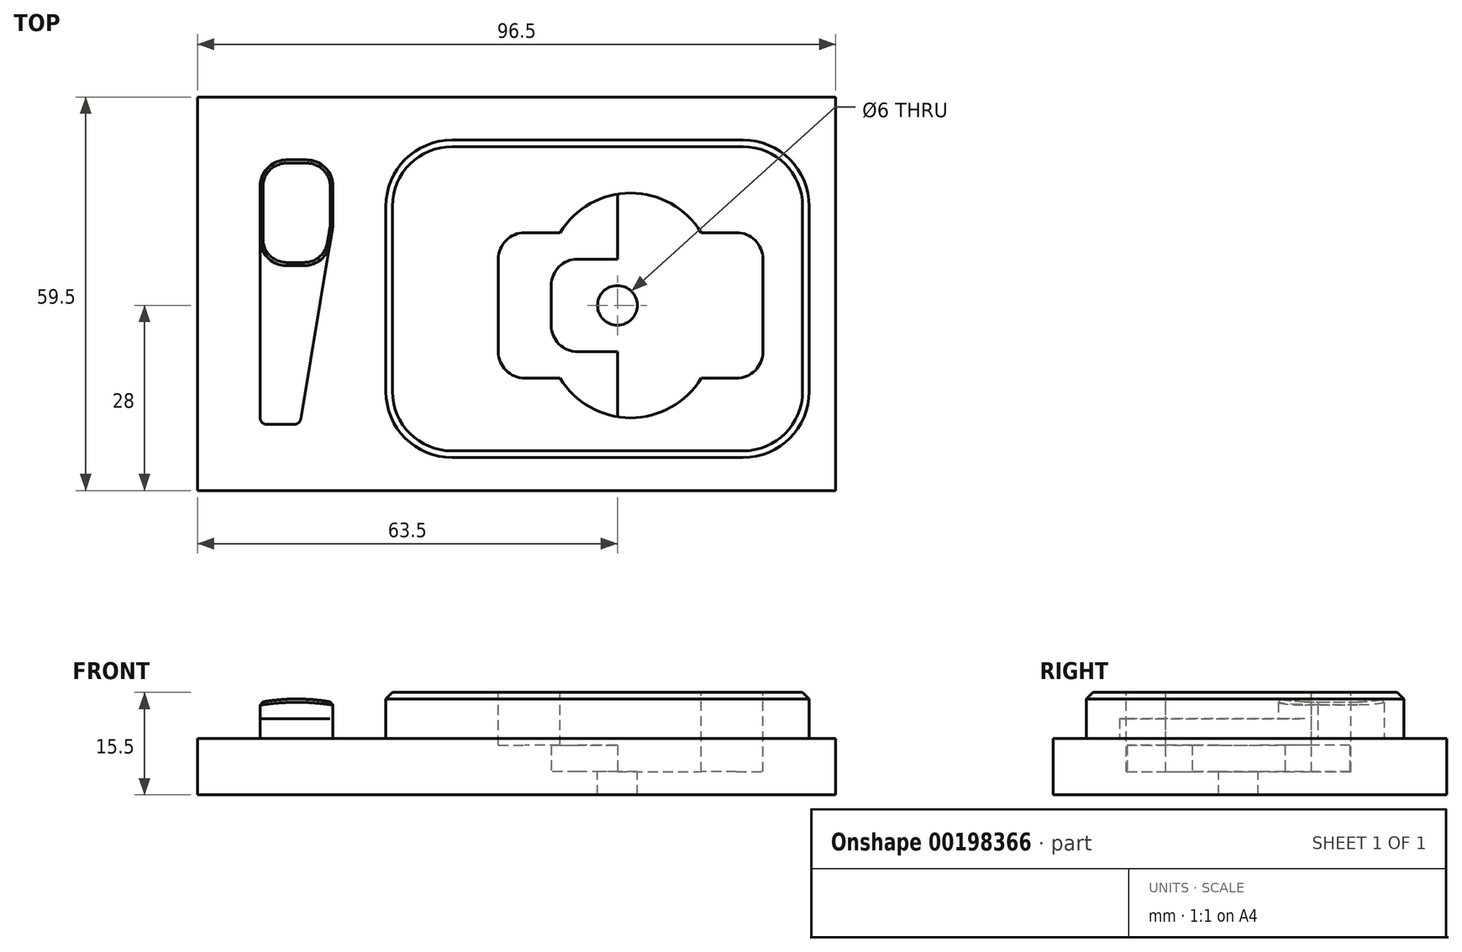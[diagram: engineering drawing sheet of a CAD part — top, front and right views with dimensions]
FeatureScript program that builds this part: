
annotation { "Feature Type Name" : "Feature", "Feature Type Description" : "" }
export const myFeature = defineFeature(function(context is Context, id is Id, definition is map)
    precondition{}
    {
        {
            var Q0;
            Q0=qCreatedBy(makeId("Top.planeOp"),FACE);
            var sketch = newSketch(context, id + "F0", { "sketchPlane" : qUnion([Q0])});
            skLineSegment(sketch, "E0.bottom", {"start": v(0, 0) * mm, "end": v(-96.5, 0) * mm});
            skLineSegment(sketch, "E0.top", {"start": v(0, 59.5) * mm, "end": v(-96.5, 59.5) * mm});
            skLineSegment(sketch, "E0.left", {"start": v(0, 0) * mm, "end": v(0, 59.5) * mm});
            skLineSegment(sketch, "E0.right", {"start": v(-96.5, 0) * mm, "end": v(-96.5, 59.5) * mm});
            skSolve(sketch);
        }
        {
            var Q0;
            Q0 = qSketchRegion(id + "F0", true);
            extrude(context, id + "F1", {"entities" : qUnion([Q0]), "oppositeDirection" : true, "depth" : 15.5 * mm, "offsetDistance" : 25 * mm});
        }
        {
            var Q0;
            Q0=makeQuery(id+"F1.opExtrude","CAP_FACE",FACE,{"disambiguationData":[OSD([sQuery(id+"F0.wireOp",EDGE,"E0.bottom"),sQuery(id+"F0.wireOp",EDGE,"E0.top"),sQuery(id+"F0.wireOp",EDGE,"E0.left"),sQuery(id+"F0.wireOp",EDGE,"E0.right")])],"isStart":true});
            var sketch = newSketch(context, id + "F2", { "sketchPlane" : qUnion([Q0])});
            skLineSegment(sketch, "E1.bottom", {"start": v(-4, 5) * mm, "end": v(-68, 5) * mm});
            skLineSegment(sketch, "E1.top", {"start": v(-4, 53) * mm, "end": v(-68, 53) * mm});
            skLineSegment(sketch, "E1.left", {"start": v(-4, 5) * mm, "end": v(-4, 53) * mm});
            skLineSegment(sketch, "E1.right", {"start": v(-68, 5) * mm, "end": v(-68, 53) * mm});
            skLineSegment(sketch, "E2.bottom", {"start": v(-11, 17) * mm, "end": v(-20.32, 17) * mm});
            skLineSegment(sketch, "E2.top", {"start": v(-11, 39) * mm, "end": v(-20.32, 39) * mm});
            skLineSegment(sketch, "E2.left", {"start": v(-11, 17) * mm, "end": v(-11, 39) * mm});
            skLineSegment(sketch, "E2.right", {"start": v(-51, 17) * mm, "end": v(-51, 39) * mm});
            skLineSegment(sketch, "E3", {"start": v(-51, 28) * mm, "end": v(-11, 28) * mm, "construction": true});
            skLineSegment(sketch, "E4", {"start": v(-31, 39) * mm, "end": v(-31, 17) * mm, "construction": true});
            skArc(sketch, "E5", {"start": v(-20.32, 17) * mm, "mid": v(-31, 11) * mm, "end": v(-41.68, 17) * mm});
            skArc(sketch, "E6.MirrorCS", {"start": v(-20.32, 39) * mm, "mid": v(-31, 45) * mm, "end": v(-41.68, 39) * mm});
            skLineSegment(sketch, "E7.trimOffspring", {"start": v(-41.68, 39) * mm, "end": v(-51, 39) * mm});
            skLineSegment(sketch, "E8.trimOffspring", {"start": v(-41.68, 17) * mm, "end": v(-51, 17) * mm});
            skSolve(sketch);
        }
        {
            var Q0;
            Q0=makeQuery(id+"F2.imprint","IMPRINT",FACE,{"disambiguationData":[TD([[makeQuery(id+"F2.imprint","IMPRINT",EDGE,{"derivedFrom":sQuery(id+"F2.wireOp",EDGE,"E1.bottom")}),1.0]])]});
            extrude(context, id + "F3", {"entities" : qUnion([Q0]), "operationType" : NewBodyOperationType.REMOVE, "oppositeDirection" : true, "depth" : (15.5 - 8.5) * mm, "offsetDistance" : 25 * mm});
        }
        {
            var Q0;
            Q0=makeQuery(id+"F2.imprint","IMPRINT",FACE,{"disambiguationData":[TD([[makeQuery(id+"F2.imprint","IMPRINT",EDGE,{"derivedFrom":sQuery(id+"F2.wireOp",EDGE,"E2.bottom")}),-1.0]])]});
            extrude(context, id + "F4", {"entities" : qUnion([Q0]), "operationType" : NewBodyOperationType.REMOVE, "oppositeDirection" : true, "depth" : 12 * mm, "offsetDistance" : 25 * mm});
        }
        {
            var Q0;
            Q0=makeQuery(id+"F4.boolean.opBoolean","COPY",FACE,{"derivedFrom":makeQuery(id+"F4.opExtrude","CAP_FACE",FACE,{"disambiguationData":[OSD([sQuery(id+"F2.wireOp",EDGE,"E2.bottom"),sQuery(id+"F2.wireOp",EDGE,"E2.top"),sQuery(id+"F2.wireOp",EDGE,"E2.left"),sQuery(id+"F2.wireOp",EDGE,"E2.right"),sQuery(id+"F2.wireOp",EDGE,"E5"),sQuery(id+"F2.wireOp",EDGE,"E6.MirrorCS"),sQuery(id+"F2.wireOp",EDGE,"E7.trimOffspring"),sQuery(id+"F2.wireOp",EDGE,"E8.trimOffspring")])],"isStart":false})});
            var sketch = newSketch(context, id + "F5", { "sketchPlane" : qUnion([Q0])});
            skLineSegment(sketch, "E9", {"start": v(-51, 28) * mm, "end": v(-11, 28) * mm, "construction": true});
            skLineSegment(sketch, "E10", {"start": v(-33, 44.84) * mm, "end": v(-33, 35) * mm});
            skLineSegment(sketch, "E11", {"start": v(-33, 35) * mm, "end": v(-43, 35) * mm});
            skLineSegment(sketch, "E12", {"start": v(-43, 35) * mm, "end": v(-43, 28) * mm});
            skLineSegment(sketch, "E13.MirrorCS", {"start": v(-43, 21) * mm, "end": v(-43, 28) * mm});
            skLineSegment(sketch, "E14.MirrorCS", {"start": v(-33, 21) * mm, "end": v(-43, 21) * mm});
            skLineSegment(sketch, "E15.MirrorCS", {"start": v(-33, 11.16) * mm, "end": v(-33, 21) * mm});
            skPoint(sketch, "E16", {"position": v(-33, 28) * mm});
            skSolve(sketch);
        }
        {
            var Q0;
            {var subQ3=sQuery(id+"F5.wireOp",EDGE,"E10");Q0=makeQuery(id+"F5.imprint","IMPRINT",FACE,{"disambiguationData":[TD([[makeQuery(id+"F5.imprint","IMPRINT",EDGE,{"derivedFrom":subQ3}),-1.0]])]});}
            extrude(context, id + "F6", {"entities" : qUnion([Q0]), "operationType" : NewBodyOperationType.ADD, "depth" : (12 - 8) * mm, "offsetDistance" : 25 * mm});
        }
        {
            var Q0;
            Q0=sQuery(id+"F5.wireOp",VERTEX,"E16");
            var Q1;
            Q1=makeQuery(id+"F1.opExtrude","SWEPT_BODY",BODY,{"disambiguationData":[OSD([sQuery(id+"F0.wireOp",EDGE,"E0.bottom"),sQuery(id+"F0.wireOp",EDGE,"E0.top"),sQuery(id+"F0.wireOp",EDGE,"E0.left"),sQuery(id+"F0.wireOp",EDGE,"E0.right")])]});
            hole(context, id + "F7", {"style" : HoleStyle.SIMPLE, "endStyle" : HoleEndStyle.THROUGH, "holeDiameter" : 6 * mm, "majorDiameter" : 5 * mm, "tappedDepth" : 12 * mm, "tapClearance" : 3, "startFromSketch" : true, "locations" : qUnion([Q0]), "scope" : qUnion([Q1])});
        }
        {
            var Q0;
            Q0=makeQuery(id+"F3.boolean.opBoolean","COPY",EDGE,{"derivedFrom":makeQuery(id+"F3.opExtrude","SWEPT_EDGE",EDGE,{"disambiguationData":[OSD([sQuery(id+"F2.wireOp",EDGE,"E1.bottom"),sQuery(id+"F2.wireOp",EDGE,"E1.right")])]})});
            var Q1;
            Q1=makeQuery(id+"F3.boolean.opBoolean","COPY",EDGE,{"derivedFrom":makeQuery(id+"F3.opExtrude","SWEPT_EDGE",EDGE,{"disambiguationData":[OSD([sQuery(id+"F2.wireOp",EDGE,"E1.bottom"),sQuery(id+"F2.wireOp",EDGE,"E1.left")])]})});
            var Q2;
            Q2=makeQuery(id+"F3.boolean.opBoolean","COPY",EDGE,{"derivedFrom":makeQuery(id+"F3.opExtrude","SWEPT_EDGE",EDGE,{"disambiguationData":[OSD([sQuery(id+"F2.wireOp",EDGE,"E1.top"),sQuery(id+"F2.wireOp",EDGE,"E1.left")])]})});
            var Q3;
            Q3=makeQuery(id+"F3.boolean.opBoolean","COPY",EDGE,{"derivedFrom":makeQuery(id+"F3.opExtrude","SWEPT_EDGE",EDGE,{"disambiguationData":[OSD([sQuery(id+"F2.wireOp",EDGE,"E1.top"),sQuery(id+"F2.wireOp",EDGE,"E1.right")])]})});
            fillet(context, id + "F8", {"entities" : qUnion([Q0, Q1, Q2, Q3]), "tangentPropagation" : true, "radius" : 10 * mm, "defaultsChanged" : false, "vertexSettings" : [], "allowEdgeOverflow" : false});
        }
        {
            var Q0;
            Q0=makeQuery(id+"F4.boolean.opBoolean","COPY",EDGE,{"derivedFrom":makeQuery(id+"F4.opExtrude","SWEPT_EDGE",EDGE,{"disambiguationData":[OSD([sQuery(id+"F2.wireOp",EDGE,"E2.right"),sQuery(id+"F2.wireOp",EDGE,"E7.trimOffspring")])]})});
            var Q1;
            Q1=makeQuery(id+"F4.boolean.opBoolean","COPY",EDGE,{"derivedFrom":makeQuery(id+"F4.opExtrude","SWEPT_EDGE",EDGE,{"disambiguationData":[OSD([sQuery(id+"F2.wireOp",EDGE,"E2.top"),sQuery(id+"F2.wireOp",EDGE,"E2.left")])]})});
            var Q2;
            Q2=makeQuery(id+"F4.boolean.opBoolean","COPY",EDGE,{"derivedFrom":makeQuery(id+"F4.opExtrude","SWEPT_EDGE",EDGE,{"disambiguationData":[OSD([sQuery(id+"F2.wireOp",EDGE,"E2.bottom"),sQuery(id+"F2.wireOp",EDGE,"E2.left")])]})});
            var Q3;
            Q3=makeQuery(id+"F4.boolean.opBoolean","COPY",EDGE,{"derivedFrom":makeQuery(id+"F4.opExtrude","SWEPT_EDGE",EDGE,{"disambiguationData":[OSD([sQuery(id+"F2.wireOp",EDGE,"E2.right"),sQuery(id+"F2.wireOp",EDGE,"E8.trimOffspring")])]})});
            var Q4;
            Q4=makeQuery(id+"F6.opExtrude","SWEPT_EDGE",EDGE,{"disambiguationData":[OSD([sQuery(id+"F5.wireOp",EDGE,"E13.MirrorCS"),sQuery(id+"F5.wireOp",EDGE,"E14.MirrorCS")])]});
            var Q5;
            Q5=makeQuery(id+"F6.opExtrude","SWEPT_EDGE",EDGE,{"disambiguationData":[OSD([sQuery(id+"F5.wireOp",EDGE,"E11"),sQuery(id+"F5.wireOp",EDGE,"E12")])]});
            var Q6;
            Q6=makeQuery(id+"F6.opExtrude","SWEPT_EDGE",EDGE,{"disambiguationData":[OSD([sQuery(id+"F2.wireOp",EDGE,"E6.MirrorCS"),sQuery(id+"F5.wireOp",EDGE,"E10")])]});
            var Q7;
            Q7=makeQuery(id+"F6.opExtrude","SWEPT_EDGE",EDGE,{"disambiguationData":[OSD([sQuery(id+"F2.wireOp",EDGE,"E5"),sQuery(id+"F5.wireOp",EDGE,"E15.MirrorCS")])]});
            fillet(context, id + "F9", {"entities" : qUnion([Q0, Q1, Q2, Q3, Q4, Q5, Q6, Q7]), "tangentPropagation" : true, "radius" : 4 * mm, "defaultsChanged" : false, "vertexSettings" : [], "allowEdgeOverflow" : false});
        }
        {
            var Q0;
            Q0=makeQuery(id+"F8.opFillet","BLEND_EDGE",EDGE,{"blendedFrom":[makeQuery(id+"F3.boolean.opBoolean","COPY",EDGE,{"derivedFrom":makeQuery(id+"F3.opExtrude","SWEPT_EDGE",EDGE,{"disambiguationData":[OSD([sQuery(id+"F2.wireOp",EDGE,"E1.top"),sQuery(id+"F2.wireOp",EDGE,"E1.right")])]})}),makeQuery(id+"F1.opExtrude","CAP_FACE",FACE,{"disambiguationData":[OSD([sQuery(id+"F0.wireOp",EDGE,"E0.bottom"),sQuery(id+"F0.wireOp",EDGE,"E0.top"),sQuery(id+"F0.wireOp",EDGE,"E0.left"),sQuery(id+"F0.wireOp",EDGE,"E0.right")])],"isStart":true})],"blendedInto":[makeQuery(id+"F1.opExtrude","CAP_FACE",FACE,{"disambiguationData":[OSD([sQuery(id+"F0.wireOp",EDGE,"E0.bottom"),sQuery(id+"F0.wireOp",EDGE,"E0.top"),sQuery(id+"F0.wireOp",EDGE,"E0.left"),sQuery(id+"F0.wireOp",EDGE,"E0.right")])],"isStart":true})]});
            chamfer(context, id + "F10", {"entities" : qUnion([Q0]), "width" : 1 * mm, "tangentPropagation" : true});
        }
        {
            var Q0;
            Q0=makeQuery(id+"F3.boolean.opBoolean","COPY",FACE,{"derivedFrom":makeQuery(id+"F3.opExtrude","CAP_FACE",FACE,{"disambiguationData":[OSD([sQuery(id+"F0.wireOp",EDGE,"E0.bottom"),sQuery(id+"F0.wireOp",EDGE,"E0.top"),sQuery(id+"F0.wireOp",EDGE,"E0.left"),sQuery(id+"F0.wireOp",EDGE,"E0.right"),sQuery(id+"F2.wireOp",EDGE,"E1.bottom"),sQuery(id+"F2.wireOp",EDGE,"E1.top"),sQuery(id+"F2.wireOp",EDGE,"E1.left"),sQuery(id+"F2.wireOp",EDGE,"E1.right")])],"isStart":false})});
            var sketch = newSketch(context, id + "F11", { "sketchPlane" : qUnion([Q0])});
            skLineSegment(sketch, "E17", {"start": v(-76, 50) * mm, "end": v(-87, 50) * mm});
            skLineSegment(sketch, "E18", {"start": v(-87, 50) * mm, "end": v(-87, 10) * mm});
            skLineSegment(sketch, "E19", {"start": v(-87, 10) * mm, "end": v(-81, 10) * mm});
            skLineSegment(sketch, "E20", {"start": v(-81, 10) * mm, "end": v(-76, 40) * mm});
            skLineSegment(sketch, "E21", {"start": v(-76, 40) * mm, "end": v(-76, 50) * mm});
            skLineSegment(sketch, "E22", {"start": v(-87, 34) * mm, "end": v(-77, 34) * mm});
            skSolve(sketch);
        }
        {
            var Q0;
            {var subQ0=sQuery(id+"F11.wireOp",EDGE,"E19");Q0=makeQuery(id+"F11.imprint","IMPRINT",FACE,{"disambiguationData":[TD([[makeQuery(id+"F11.imprint","IMPRINT",EDGE,{"derivedFrom":subQ0}),1.0]])]});}
            extrude(context, id + "F12", {"entities" : qUnion([Q0]), "operationType" : NewBodyOperationType.ADD, "depth" : 3 * mm, "offsetDistance" : 25 * mm});
        }
        {
            var Q0;
            {var subQ2=sQuery(id+"F11.wireOp",EDGE,"E17");Q0=makeQuery(id+"F11.imprint","IMPRINT",FACE,{"disambiguationData":[TD([[makeQuery(id+"F11.imprint","IMPRINT",EDGE,{"derivedFrom":subQ2}),1.0]])]});}
            extrude(context, id + "F13", {"entities" : qUnion([Q0]), "operationType" : NewBodyOperationType.ADD, "depth" : (14.5 - 8.5) * mm, "offsetDistance" : 25 * mm});
        }
        {
            var Q0;
            Q0=makeQuery(id+"F13.opExtrude","SWEPT_EDGE",EDGE,{"disambiguationData":[OSD([sQuery(id+"F11.wireOp",EDGE,"E17"),sQuery(id+"F11.wireOp",EDGE,"E18")])]});
            var Q1;
            Q1=makeQuery(id+"F13.opExtrude","SWEPT_EDGE",EDGE,{"disambiguationData":[OSD([sQuery(id+"F11.wireOp",EDGE,"E17"),sQuery(id+"F11.wireOp",EDGE,"E21")])]});
            var Q2;
            Q2=makeQuery(id+"F13.opExtrude","SWEPT_EDGE",EDGE,{"disambiguationData":[OSD([sQuery(id+"F11.wireOp",EDGE,"E18"),sQuery(id+"F11.wireOp",EDGE,"E22")])]});
            var Q3;
            Q3=makeQuery(id+"F13.opExtrude","SWEPT_EDGE",EDGE,{"disambiguationData":[OSD([sQuery(id+"F11.wireOp",EDGE,"E20"),sQuery(id+"F11.wireOp",EDGE,"E22")])]});
            fillet(context, id + "F14", {"entities" : qUnion([Q0, Q1, Q2, Q3]), "tangentPropagation" : true, "radius" : 4 * mm, "defaultsChanged" : false, "vertexSettings" : [], "allowEdgeOverflow" : false});
        }
        {
            var Q0;
            Q0=makeQuery(id+"F12.opExtrude","SWEPT_EDGE",EDGE,{"disambiguationData":[OSD([sQuery(id+"F11.wireOp",EDGE,"E18"),sQuery(id+"F11.wireOp",EDGE,"E19")])]});
            var Q1;
            Q1=makeQuery(id+"F12.opExtrude","SWEPT_EDGE",EDGE,{"disambiguationData":[OSD([sQuery(id+"F11.wireOp",EDGE,"E19"),sQuery(id+"F11.wireOp",EDGE,"E20")])]});
            fillet(context, id + "F15", {"entities" : qUnion([Q0, Q1]), "tangentPropagation" : true, "radius" : 1 * mm, "defaultsChanged" : false, "vertexSettings" : [], "allowEdgeOverflow" : false});
        }
        {
            var Q0;
            Q0=makeQuery(id+"F13.opExtrude","SWEPT_FACE",FACE,{"disambiguationData":[OSD([sQuery(id+"F11.wireOp",EDGE,"E17")])]});
            var sketch = newSketch(context, id + "F16", { "sketchPlane" : qUnion([Q0])});
            skArc(sketch, "E23", {"start": v(73.31, -2.14) * mm, "mid": v(81.5, -1) * mm, "end": v(89.69, -2.14) * mm});
            skPoint(sketch, "E23.centerSnap0", {"position": v(81.5, -7) * mm});
            skLineSegment(sketch, "E24", {"start": v(73.31, -2.14) * mm, "end": v(73.31, 2.88) * mm});
            skLineSegment(sketch, "E25", {"start": v(73.31, 2.88) * mm, "end": v(89.69, 2.88) * mm});
            skLineSegment(sketch, "E26", {"start": v(89.69, 2.88) * mm, "end": v(89.69, -2.14) * mm});
            skSolve(sketch);
        }
        {
            var Q0;
            Q0 = qSketchRegion(id + "F16", true);
            extrude(context, id + "F17", {"entities" : qUnion([Q0]), "operationType" : NewBodyOperationType.REMOVE, "endBound" : BoundingType.THROUGH_ALL, "oppositeDirection" : true, "depth" : 25 * mm, "offsetDistance" : 25 * mm});
        }
        {
            var Q0;
            Q0=makeQuery(id+"F17.boolean.opBoolean","INTERSECT",EDGE,{"derivedFrom":[makeQuery(id+"F14.opFillet","BLEND_FACE",FACE,{"disambiguationData":[OSD([sQuery(id+"F11.wireOp",EDGE,"E20"),sQuery(id+"F11.wireOp",EDGE,"E22")])]}),makeQuery(id+"F17.opExtrude","SWEPT_FACE",FACE,{"disambiguationData":[OSD([sQuery(id+"F16.wireOp",EDGE,"E23")])]})]});
            chamfer(context, id + "F18", {"entities" : qUnion([Q0]), "width" : 0.5 * mm, "tangentPropagation" : true});
        }
    });
